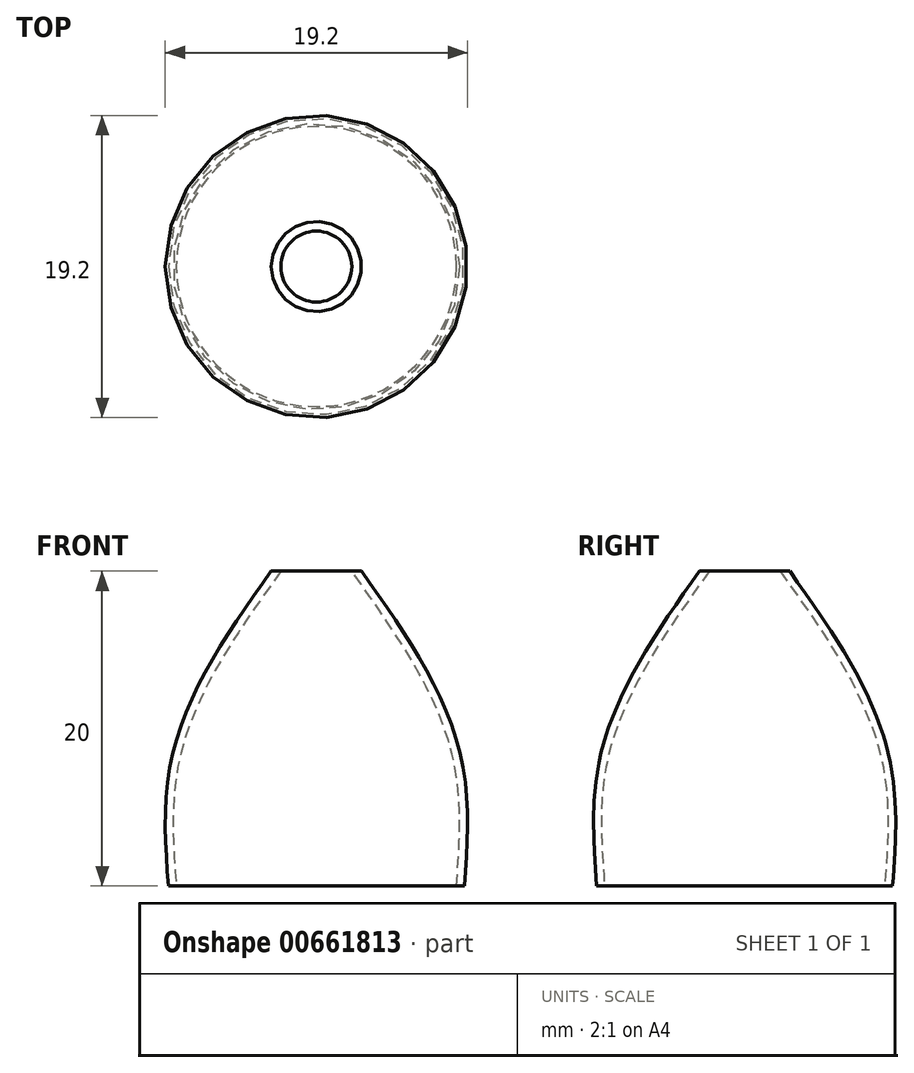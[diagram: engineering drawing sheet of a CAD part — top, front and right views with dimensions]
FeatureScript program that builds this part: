
annotation { "Feature Type Name" : "Feature", "Feature Type Description" : "" }
export const myFeature = defineFeature(function(context is Context, id is Id, definition is map)
    precondition{}
    {
        {
            var Q0;
            Q0=qCreatedBy(makeId("Top.planeOp"),FACE);
            var sketch = newSketch(context, id + "F0", { "sketchPlane" : qUnion([Q0])});
            skCircle(sketch, "E0", {"center": v(0, 0) * mm, "radius": 8.9 * mm});
            skSolve(sketch);
        }
        {
            var Q0;
            Q0=qCreatedBy(makeId("Top.planeOp"),FACE);
            cPlane(context, id + "F1", {"entities" : qUnion([Q0]), "cplaneType" : CPlaneType.OFFSET, "offset" : 7 * mm, "width" : 150 * mm, "height" : 150 * mm});
        }
        {
            var Q0;
            Q0=qCreatedBy(id+"F1.planeOp",FACE);
            cPlane(context, id + "F2", {"entities" : qUnion([Q0]), "cplaneType" : CPlaneType.OFFSET, "offset" : 13 * mm, "width" : 150 * mm, "height" : 150 * mm});
        }
        {
            var Q0;
            Q0=qCreatedBy(id+"F2.planeOp",FACE);
            var sketch = newSketch(context, id + "F3", { "sketchPlane" : qUnion([Q0])});
            skCircle(sketch, "E1", {"center": v(0, 0) * mm, "radius": 2.25 * mm});
            skSolve(sketch);
        }
        {
            var Q0;
            Q0=qCreatedBy(id+"F1.planeOp",FACE);
            var sketch = newSketch(context, id + "F4", { "sketchPlane" : qUnion([Q0])});
            skCircle(sketch, "E2", {"center": v(0, 0) * mm, "radius": 8.9 * mm});
            skSolve(sketch);
        }
        {
            var Q0;
            Q0 = qSketchRegion(id + "F0", true);
            var Q1;
            Q1 = qSketchRegion(id + "F4", true);
            var Q2;
            Q2 = qSketchRegion(id + "F3", true);
            loft(context, id + "F5", {"sheetProfilesArray" : [{ "sheetProfileEntities" : qUnion([Q0]) }, { "sheetProfileEntities" : qUnion([Q1]) }, { "sheetProfileEntities" : qUnion([Q2]) }]});
        }
        {
            var Q0;
            Q0=makeQuery(id+"F5.opLoft","CAP_FACE",FACE,{"disambiguationData":[OSD([makeQuery(id+"F0.imprint","IMPRINT",FACE,{"disambiguationData":[TD([[makeQuery(id+"F0.imprint","IMPRINT",EDGE,{"derivedFrom":sQuery(id+"F0.wireOp",EDGE,"E0")}),1.0]])]})])],"isStart":true});
            var Q1;
            Q1=makeQuery(id+"F5.opLoft","CAP_FACE",FACE,{"disambiguationData":[OSD([makeQuery(id+"F3.imprint","IMPRINT",FACE,{"disambiguationData":[TD([[makeQuery(id+"F3.imprint","IMPRINT",EDGE,{"derivedFrom":sQuery(id+"F3.wireOp",EDGE,"E1")}),1.0]])]})])],"isStart":true});
            shell(context, id + "F6", {"entities" : qUnion([Q0, Q1]), "thickness" : .5 * mm, "oppositeDirection" : true});
        }
    });
